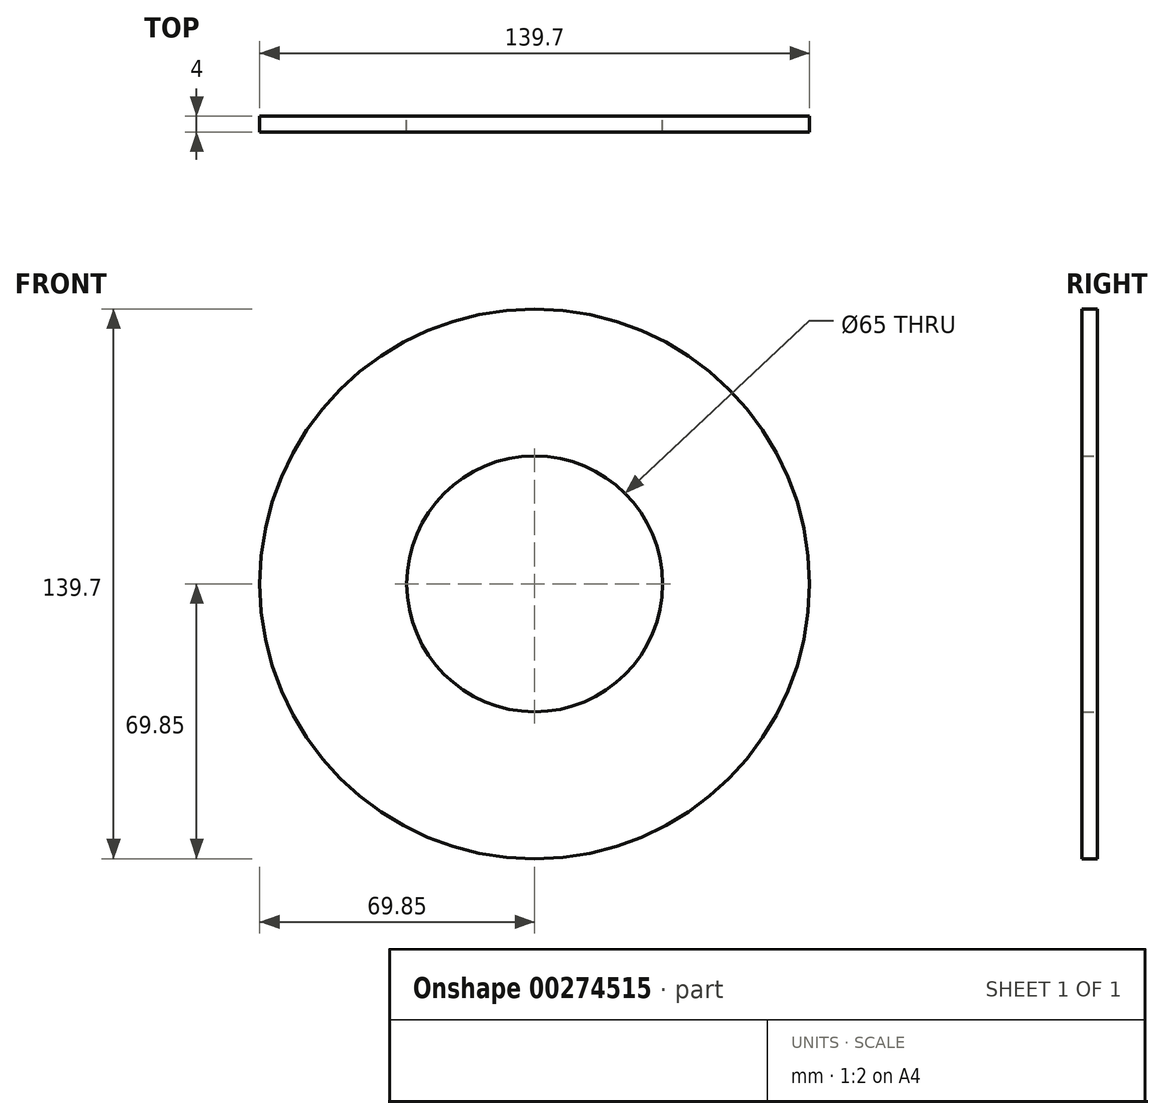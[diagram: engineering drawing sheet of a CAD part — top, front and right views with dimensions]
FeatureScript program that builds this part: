
annotation { "Feature Type Name" : "Feature", "Feature Type Description" : "" }
export const myFeature = defineFeature(function(context is Context, id is Id, definition is map)
    precondition{}
    {
        {
            var Q0;
            Q0=qCreatedBy(makeId("Front.planeOp"),FACE);
            var sketch = newSketch(context, id + "F0", { "sketchPlane" : qUnion([Q0])});
            skCircle(sketch, "E0", {"center": v(0, 0) * mm, "radius": 69.85 * mm});
            skCircle(sketch, "E1", {"center": v(0, 0) * mm, "radius": 32.5 * mm});
            skSolve(sketch);
        }
        {
            var Q0;
            Q0 = qSketchRegion(id + "F0", true);
            extrude(context, id + "F1", {"entities" : qUnion([Q0]), "depth" : 4 * mm});
        }
    });
